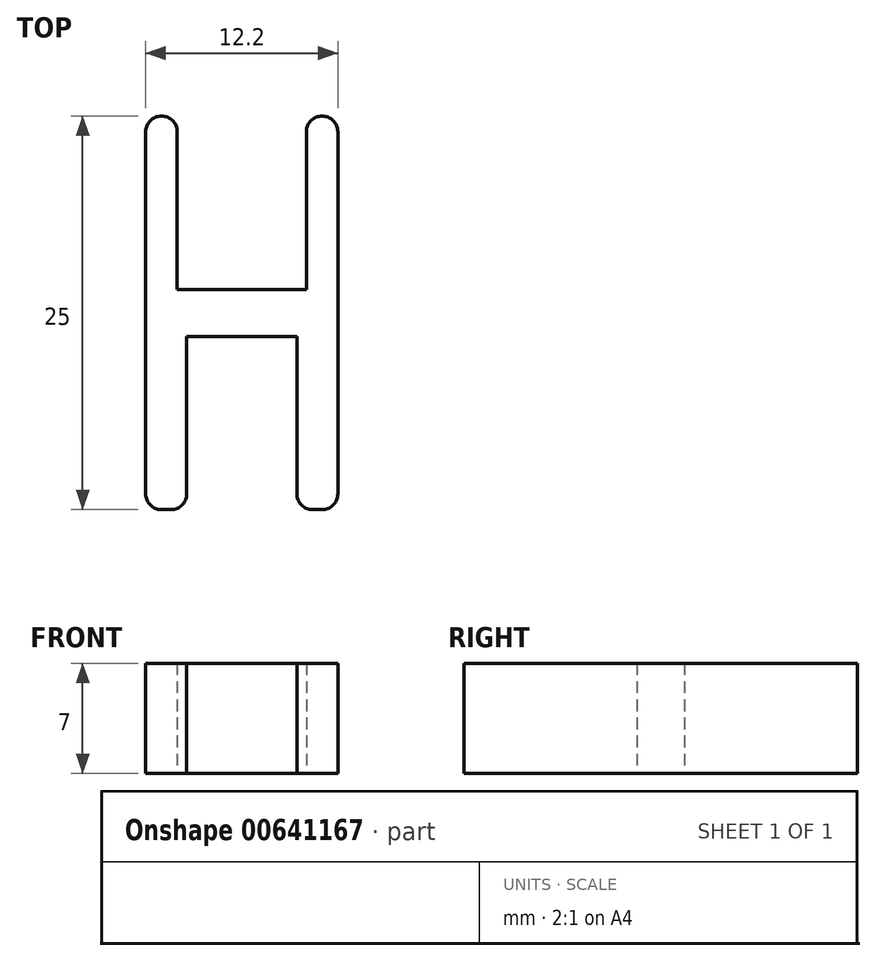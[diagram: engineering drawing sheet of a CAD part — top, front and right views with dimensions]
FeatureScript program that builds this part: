
annotation { "Feature Type Name" : "Feature", "Feature Type Description" : "" }
export const myFeature = defineFeature(function(context is Context, id is Id, definition is map)
    precondition{}
    {
        {
            var Q0;
            Q0=qCreatedBy(makeId("Top.planeOp"),FACE);
            var sketch = newSketch(context, id + "F0", { "sketchPlane" : qUnion([Q0])});
            skLineSegment(sketch, "E0", {"start": v(0, 1.5) * mm, "end": v(-4.1, 1.5) * mm});
            skLineSegment(sketch, "E1", {"start": v(-4.1, 1.5) * mm, "end": v(-4.1, 12.5) * mm});
            skLineSegment(sketch, "E2", {"start": v(-4.1, 12.5) * mm, "end": v(-6.1, 12.5) * mm});
            skLineSegment(sketch, "E3", {"start": v(-6.1, 12.5) * mm, "end": v(-6.1, -12.5) * mm});
            skLineSegment(sketch, "E4", {"start": v(-6.1, -12.5) * mm, "end": v(-3.5, -12.5) * mm});
            skLineSegment(sketch, "E5", {"start": v(-3.5, -12.5) * mm, "end": v(-3.5, -1.5) * mm});
            skLineSegment(sketch, "E6", {"start": v(-3.5, -1.5) * mm, "end": v(0, -1.5) * mm});
            skLineSegment(sketch, "E7.MirrorCS", {"start": v(6.1, 12.5) * mm, "end": v(6.1, -12.5) * mm});
            skLineSegment(sketch, "E8.MirrorCS", {"start": v(3.5, -12.5) * mm, "end": v(3.5, -1.5) * mm});
            skLineSegment(sketch, "E9.MirrorCS", {"start": v(0, 1.5) * mm, "end": v(4.1, 1.5) * mm});
            skLineSegment(sketch, "E10.MirrorCS", {"start": v(3.5, -1.5) * mm, "end": v(0, -1.5) * mm});
            skLineSegment(sketch, "E11.MirrorCS", {"start": v(4.1, 1.5) * mm, "end": v(4.1, 12.5) * mm});
            skLineSegment(sketch, "E12.MirrorCS", {"start": v(4.1, 12.5) * mm, "end": v(6.1, 12.5) * mm});
            skLineSegment(sketch, "E13.MirrorCS", {"start": v(6.1, -12.5) * mm, "end": v(3.5, -12.5) * mm});
            skSolve(sketch);
        }
        {
            var Q0;
            Q0 = qSketchRegion(id + "F0", true);
            extrude(context, id + "F1", {"entities" : qUnion([Q0]), "depth" : 7 * mm, "offsetDistance" : 25 * mm});
        }
        {
            var Q0;
            Q0=makeQuery(id+"F1.opExtrude","SWEPT_EDGE",EDGE,{"disambiguationData":[OSD([sQuery(id+"F0.wireOp",EDGE,"E8.MirrorCS"),sQuery(id+"F0.wireOp",EDGE,"E13.MirrorCS")])]});
            var Q1;
            Q1=makeQuery(id+"F1.opExtrude","SWEPT_EDGE",EDGE,{"disambiguationData":[OSD([sQuery(id+"F0.wireOp",EDGE,"E7.MirrorCS"),sQuery(id+"F0.wireOp",EDGE,"E13.MirrorCS")])]});
            var Q2;
            Q2=makeQuery(id+"F1.opExtrude","SWEPT_EDGE",EDGE,{"disambiguationData":[OSD([sQuery(id+"F0.wireOp",EDGE,"E4"),sQuery(id+"F0.wireOp",EDGE,"E5")])]});
            var Q3;
            Q3=makeQuery(id+"F1.opExtrude","SWEPT_EDGE",EDGE,{"disambiguationData":[OSD([sQuery(id+"F0.wireOp",EDGE,"E3"),sQuery(id+"F0.wireOp",EDGE,"E4")])]});
            var Q4;
            Q4=makeQuery(id+"F1.opExtrude","SWEPT_EDGE",EDGE,{"disambiguationData":[OSD([sQuery(id+"F0.wireOp",EDGE,"E7.MirrorCS"),sQuery(id+"F0.wireOp",EDGE,"E12.MirrorCS")])]});
            var Q5;
            Q5=makeQuery(id+"F1.opExtrude","SWEPT_EDGE",EDGE,{"disambiguationData":[OSD([sQuery(id+"F0.wireOp",EDGE,"E11.MirrorCS"),sQuery(id+"F0.wireOp",EDGE,"E12.MirrorCS")])]});
            var Q6;
            Q6=makeQuery(id+"F1.opExtrude","SWEPT_EDGE",EDGE,{"disambiguationData":[OSD([sQuery(id+"F0.wireOp",EDGE,"E1"),sQuery(id+"F0.wireOp",EDGE,"E2")])]});
            var Q7;
            Q7=makeQuery(id+"F1.opExtrude","SWEPT_EDGE",EDGE,{"disambiguationData":[OSD([sQuery(id+"F0.wireOp",EDGE,"E2"),sQuery(id+"F0.wireOp",EDGE,"E3")])]});
            fillet(context, id + "F2", {"entities" : qUnion([Q0, Q1, Q2, Q3, Q4, Q5, Q6, Q7]), "radius" : 1 * mm, "tangentPropagation" : true, "allowEdgeOverflow" : false});
        }
    });
